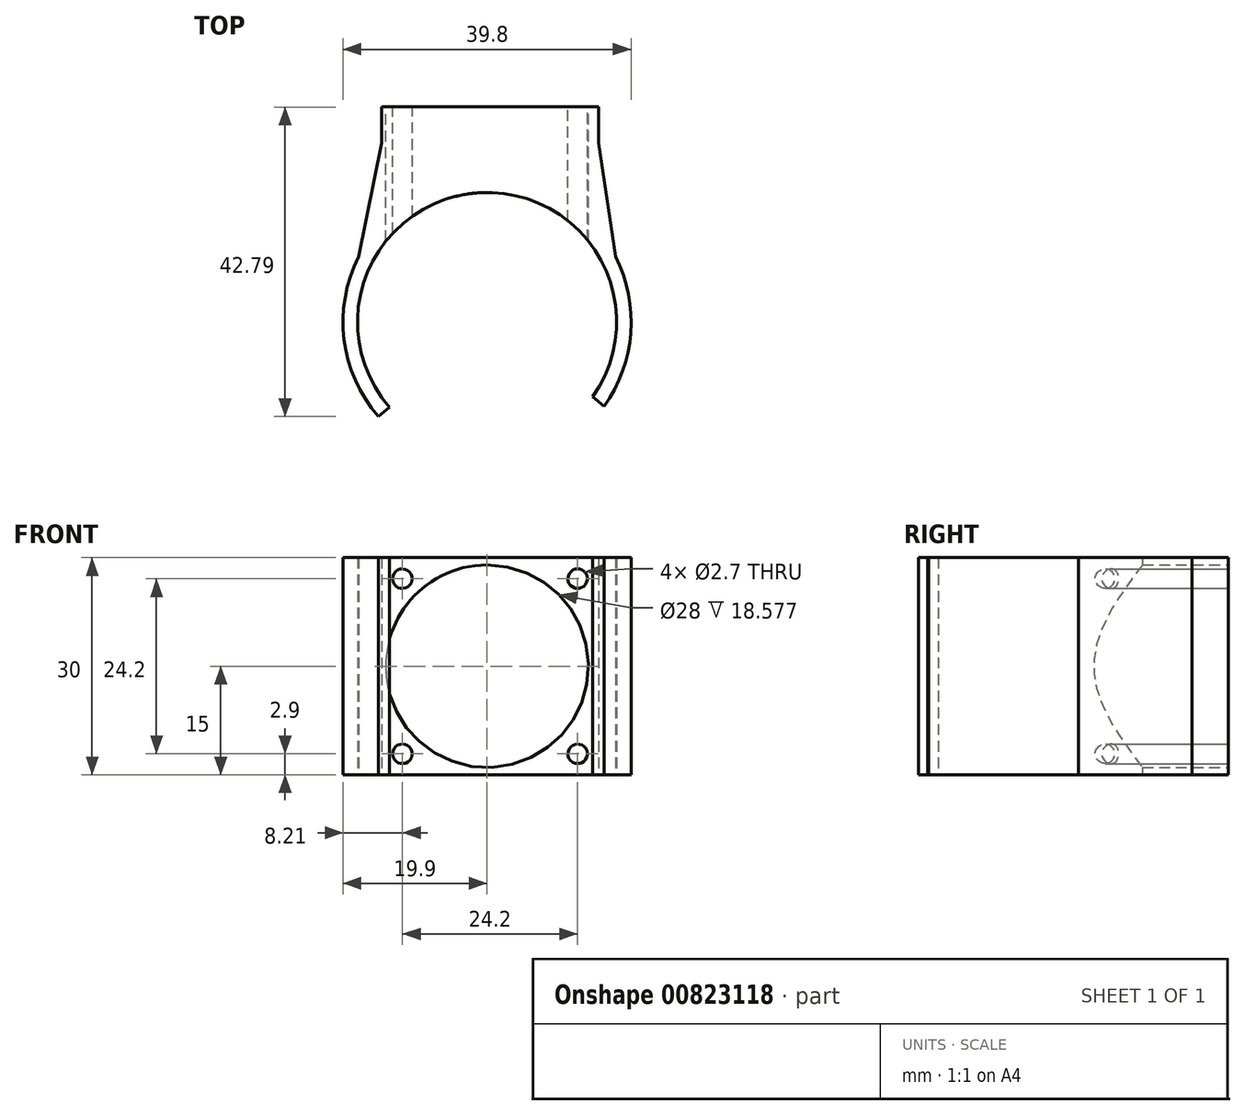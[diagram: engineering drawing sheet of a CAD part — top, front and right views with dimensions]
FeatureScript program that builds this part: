
annotation { "Feature Type Name" : "Feature", "Feature Type Description" : "" }
export const myFeature = defineFeature(function(context is Context, id is Id, definition is map)
    precondition{}
    {
        {
            var Q0;
            Q0=qCreatedBy(makeId("Top.planeOp"),FACE);
            var sketch = newSketch(context, id + "F0", { "sketchPlane" : qUnion([Q0])});
            skArc(sketch, "E0", {"start": v(14.6, -10.34) * mm, "mid": v(-0.92, 17.88) * mm, "end": v(-13.46, -11.8) * mm});
            skArc(sketch, "E1", {"start": v(-17.73, 9.04) * mm, "mid": v(-19.75, -2.43) * mm, "end": v(-15, -13.07) * mm});
            skLineSegment(sketch, "E2.bottom", {"start": v(-14.6, 29.72) * mm, "end": v(15.4, 29.72) * mm});
            skLineSegment(sketch, "E2.left", {"start": v(-14.6, 29.72) * mm, "end": v(-14.6, 24.72) * mm});
            skLineSegment(sketch, "E2.right", {"start": v(15.4, 29.72) * mm, "end": v(15.4, 24.72) * mm});
            skLineSegment(sketch, "E3", {"start": v(-14.6, 24.72) * mm, "end": v(-17.73, 9.04) * mm});
            skLineSegment(sketch, "E4", {"start": v(15.4, 24.72) * mm, "end": v(17.73, 9.04) * mm});
            skLineSegment(sketch, "E5", {"start": v(-13.46, -11.8) * mm, "end": v(-15, -13.07) * mm});
            skLineSegment(sketch, "E6", {"start": v(14.6, -10.34) * mm, "end": v(16.14, -11.64) * mm});
            skArc(sketch, "E7.trimOffspring", {"start": v(16.14, -11.64) * mm, "mid": v(19.84, -1.53) * mm, "end": v(17.73, 9.04) * mm});
            skSolve(sketch);
        }
        {
            var Q0;
            Q0=makeQuery(id+"F0.imprint","IMPRINT",FACE,{"disambiguationData":[TD([[makeQuery(id+"F0.imprint","IMPRINT",EDGE,{"derivedFrom":sQuery(id+"F0.wireOp",EDGE,"E0")}),-1.0]])]});
            extrude(context, id + "F1", {"entities" : qUnion([Q0]), "depth" : (30) * mm, "offsetDistance" : 25 * mm});
        }
        {
            var Q0;
            Q0=makeQuery(id+"F1.opExtrude","SWEPT_FACE",FACE,{"disambiguationData":[OSD([sQuery(id+"F0.wireOp",EDGE,"E2.bottom")])]});
            var sketch = newSketch(context, id + "F2", { "sketchPlane" : qUnion([Q0])});
            skCircle(sketch, "E8", {"center": v(-12.5, 27.1) * mm, "radius": 1.35 * mm});
            skCircle(sketch, "E9", {"center": v(-12.5, 2.9) * mm, "radius": 1.35 * mm});
            skCircle(sketch, "E10", {"center": v(11.7, 2.9) * mm, "radius": 1.35 * mm});
            skCircle(sketch, "E11", {"center": v(11.7, 27.1) * mm, "radius": 1.35 * mm});
            skCircle(sketch, "E12", {"center": v(0, 15) * mm, "radius": 14 * mm});
            skPoint(sketch, "E12.centerSnap0", {"position": v(-15.4, 15) * mm});
            skSolve(sketch);
        }
        {
            var Q0;
            Q0=makeQuery(id+"F2.imprint","IMPRINT",FACE,{"disambiguationData":[TD([[makeQuery(id+"F2.imprint","IMPRINT",EDGE,{"derivedFrom":sQuery(id+"F2.wireOp",EDGE,"E8")}),1.0]])]});
            var Q1;
            Q1=makeQuery(id+"F2.imprint","IMPRINT",FACE,{"disambiguationData":[TD([[makeQuery(id+"F2.imprint","IMPRINT",EDGE,{"derivedFrom":sQuery(id+"F2.wireOp",EDGE,"E9")}),1.0]])]});
            var Q2;
            Q2=makeQuery(id+"F2.imprint","IMPRINT",FACE,{"disambiguationData":[TD([[makeQuery(id+"F2.imprint","IMPRINT",EDGE,{"derivedFrom":sQuery(id+"F2.wireOp",EDGE,"E10")}),1.0]])]});
            var Q3;
            Q3=makeQuery(id+"F2.imprint","IMPRINT",FACE,{"disambiguationData":[TD([[makeQuery(id+"F2.imprint","IMPRINT",EDGE,{"derivedFrom":sQuery(id+"F2.wireOp",EDGE,"E11")}),1.0]])]});
            var Q4;
            Q4=makeQuery(id+"F2.imprint","IMPRINT",FACE,{"disambiguationData":[TD([[makeQuery(id+"F2.imprint","IMPRINT",EDGE,{"derivedFrom":sQuery(id+"F2.wireOp",EDGE,"E12")}),1.0]])]});
            extrude(context, id + "F3", {"entities" : qUnion([Q0, Q1, Q2, Q3, Q4]), "operationType" : NewBodyOperationType.REMOVE, "oppositeDirection" : true, "depth" : 25 * mm, "offsetDistance" : 25 * mm});
        }
    });
